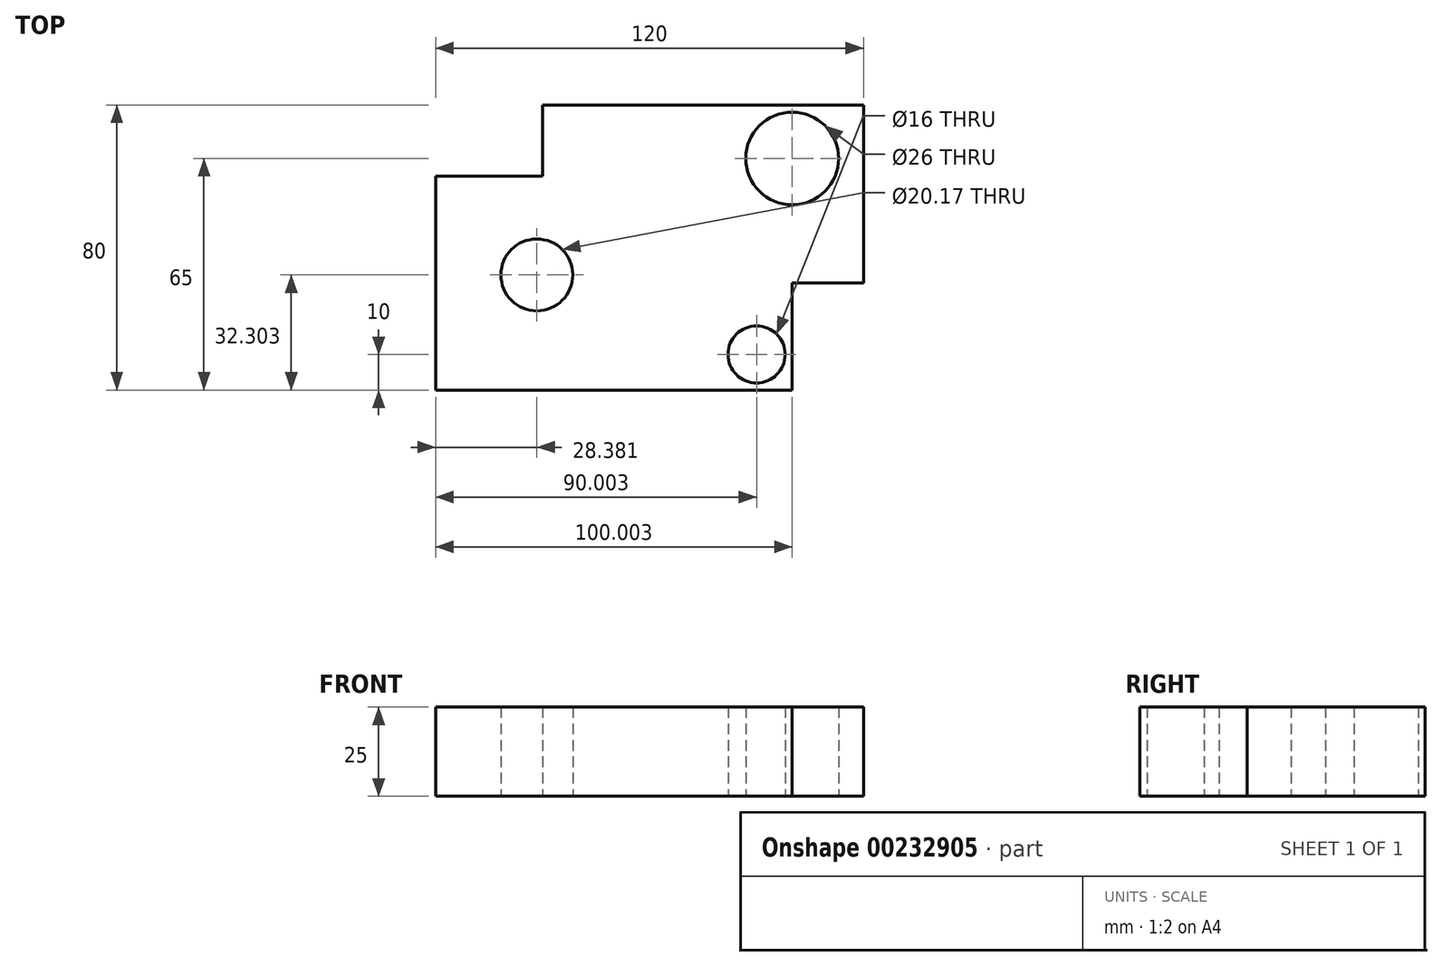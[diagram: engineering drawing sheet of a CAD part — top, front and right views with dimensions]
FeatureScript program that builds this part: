
annotation { "Feature Type Name" : "Feature", "Feature Type Description" : "" }
export const myFeature = defineFeature(function(context is Context, id is Id, definition is map)
    precondition{}
    {
        {
            var Q0;
            Q0=qCreatedBy(makeId("Top.planeOp"),FACE);
            var sketch = newSketch(context, id + "F0", { "sketchPlane" : qUnion([Q0])});
            skLineSegment(sketch, "E0", {"start": v(-157.33, 0) * mm, "end": v(-157.33, 60) * mm});
            skLineSegment(sketch, "E1", {"start": v(-157.33, 60) * mm, "end": v(-127.33, 60) * mm});
            skLineSegment(sketch, "E2", {"start": v(-127.33, 60) * mm, "end": v(-127.33, 80) * mm});
            skLineSegment(sketch, "E3", {"start": v(-127.33, 80) * mm, "end": v(-37.33, 80) * mm});
            skLineSegment(sketch, "E4", {"start": v(-37.33, 80) * mm, "end": v(-37.33, 30) * mm});
            skLineSegment(sketch, "E5", {"start": v(-37.33, 30) * mm, "end": v(-57.33, 30) * mm});
            skLineSegment(sketch, "E6", {"start": v(-57.33, 30) * mm, "end": v(-57.33, 0) * mm});
            skLineSegment(sketch, "E7", {"start": v(-57.33, 0) * mm, "end": v(-157.33, 0) * mm});
            skCircle(sketch, "E8", {"center": v(-128.95, 32.3) * mm, "radius": 10.08 * mm});
            skLineSegment(sketch, "E9", {"start": v(-128.95, 32.3) * mm, "end": v(-157.33, 32.3) * mm});
            skLineSegment(sketch, "E10", {"start": v(-157.33, 32.3) * mm, "end": v(-157.33, 0) * mm});
            skLineSegment(sketch, "E11", {"start": v(-57.33, 0) * mm, "end": v(-57.33, 10) * mm});
            skLineSegment(sketch, "E12", {"start": v(-57.33, 10) * mm, "end": v(-67.33, 10) * mm});
            skCircle(sketch, "E13", {"center": v(-67.33, 10) * mm, "radius": 8 * mm});
            skLineSegment(sketch, "E14", {"start": v(-57.33, 30) * mm, "end": v(-57.33, 65) * mm});
            skCircle(sketch, "E15", {"center": v(-57.33, 65) * mm, "radius": 13 * mm});
            skSolve(sketch);
        }
        {
            var Q0;
            Q0 = qSketchRegion(id + "F0", true);
            extrude(context, id + "F1", {"entities" : qUnion([Q0]), "depth" : 25 * mm});
        }
    });
